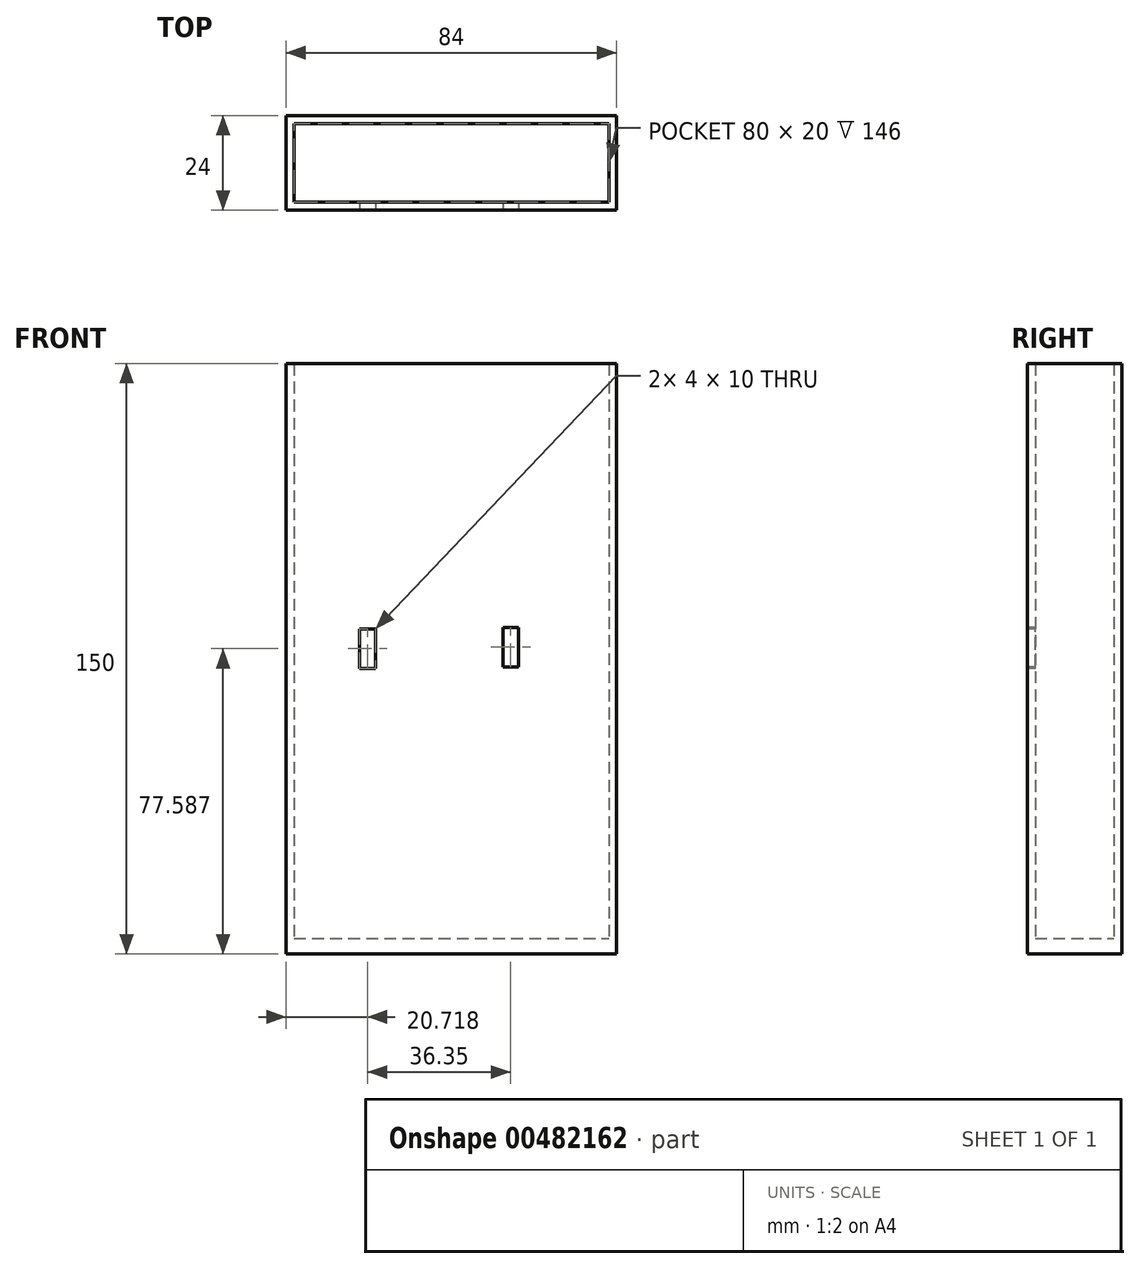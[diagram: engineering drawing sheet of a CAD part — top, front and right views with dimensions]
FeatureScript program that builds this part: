
annotation { "Feature Type Name" : "Feature", "Feature Type Description" : "" }
export const myFeature = defineFeature(function(context is Context, id is Id, definition is map)
    precondition{}
    {
        {
            var Q0;
            Q0=qCreatedBy(makeId("Top.planeOp"),FACE);
            var sketch = newSketch(context, id + "F0", { "sketchPlane" : qUnion([Q0])});
            skLineSegment(sketch, "E0.bottom", {"start": v(-40, -10) * mm, "end": v(40, -10) * mm});
            skLineSegment(sketch, "E0.top", {"start": v(-40, 10) * mm, "end": v(40, 10) * mm});
            skLineSegment(sketch, "E0.left", {"start": v(-40, -10) * mm, "end": v(-40, 10) * mm});
            skLineSegment(sketch, "E0.right", {"start": v(40, -10) * mm, "end": v(40, 10) * mm});
            skSolve(sketch);
        }
        {
            var Q0;
            Q0=qCreatedBy(makeId("Top.planeOp"),FACE);
            var sketch = newSketch(context, id + "F1", { "sketchPlane" : qUnion([Q0])});
            skLineSegment(sketch, "E1.bottom", {"start": v(-42, -12) * mm, "end": v(42, -12) * mm});
            skLineSegment(sketch, "E1.top", {"start": v(-42, 12) * mm, "end": v(42, 12) * mm});
            skLineSegment(sketch, "E1.left", {"start": v(-42, -12) * mm, "end": v(-42, 12) * mm});
            skLineSegment(sketch, "E1.right", {"start": v(42, -12) * mm, "end": v(42, 12) * mm});
            skSolve(sketch);
        }
        {
            var Q0;
            Q0=makeQuery(id+"F1.imprint","IMPRINT",FACE,{"disambiguationData":[TD([[makeQuery(id+"F1.imprint","IMPRINT",EDGE,{"derivedFrom":sQuery(id+"F1.wireOp",EDGE,"E1.bottom")}),1.0]])]});
            extrude(context, id + "F2", {"entities" : qUnion([Q0]), "depth" : 146 * mm});
        }
        {
            var Q0;
            Q0 = qSketchRegion(id + "F1", true);
            extrude(context, id + "F3", {"entities" : qUnion([Q0]), "operationType" : NewBodyOperationType.ADD, "depth" : -4 * mm});
        }
        {
            var Q0;
            Q0 = qSketchRegion(id + "F0", true);
            extrude(context, id + "F4", {"entities" : qUnion([Q0]), "operationType" : NewBodyOperationType.REMOVE, "depth" : 146 * mm});
        }
        {
            var Q0;
            {var subQ0=sQuery(id+"F1.wireOp",EDGE,"E1.bottom");Q0=makeQuery(id+"F3.boolean.opBoolean","MERGE",FACE,{"derivedFrom":[makeQuery(id+"F2.opExtrude","SWEPT_FACE",FACE,{"disambiguationData":[OSD([subQ0])]}),makeQuery(id+"F3.opExtrude","SWEPT_FACE",FACE,{"disambiguationData":[OSD([subQ0])]})]});}
            var sketch = newSketch(context, id + "F5", { "sketchPlane" : qUnion([Q0])});
            skLineSegment(sketch, "E2.bottom", {"start": v(-23.28, 78.59) * mm, "end": v(-19.28, 78.59) * mm});
            skLineSegment(sketch, "E2.top", {"start": v(-23.28, 68.59) * mm, "end": v(-19.28, 68.59) * mm});
            skLineSegment(sketch, "E2.left", {"start": v(-23.28, 78.59) * mm, "end": v(-23.28, 68.59) * mm});
            skLineSegment(sketch, "E2.right", {"start": v(-19.28, 78.59) * mm, "end": v(-19.28, 68.59) * mm});
            skLineSegment(sketch, "E3.bottom", {"start": v(13.07, 78.93) * mm, "end": v(17.07, 78.93) * mm});
            skLineSegment(sketch, "E3.top", {"start": v(13.07, 68.93) * mm, "end": v(17.07, 68.93) * mm});
            skLineSegment(sketch, "E3.left", {"start": v(13.07, 78.93) * mm, "end": v(13.07, 68.93) * mm});
            skLineSegment(sketch, "E3.right", {"start": v(17.07, 78.93) * mm, "end": v(17.07, 68.93) * mm});
            skSolve(sketch);
        }
        {
            var Q0;
            Q0 = qSketchRegion(id + "F5", true);
            extrude(context, id + "F6", {"entities" : qUnion([Q0]), "operationType" : NewBodyOperationType.REMOVE, "oppositeDirection" : true, "depth" : 3.9 * mm});
        }
    });
